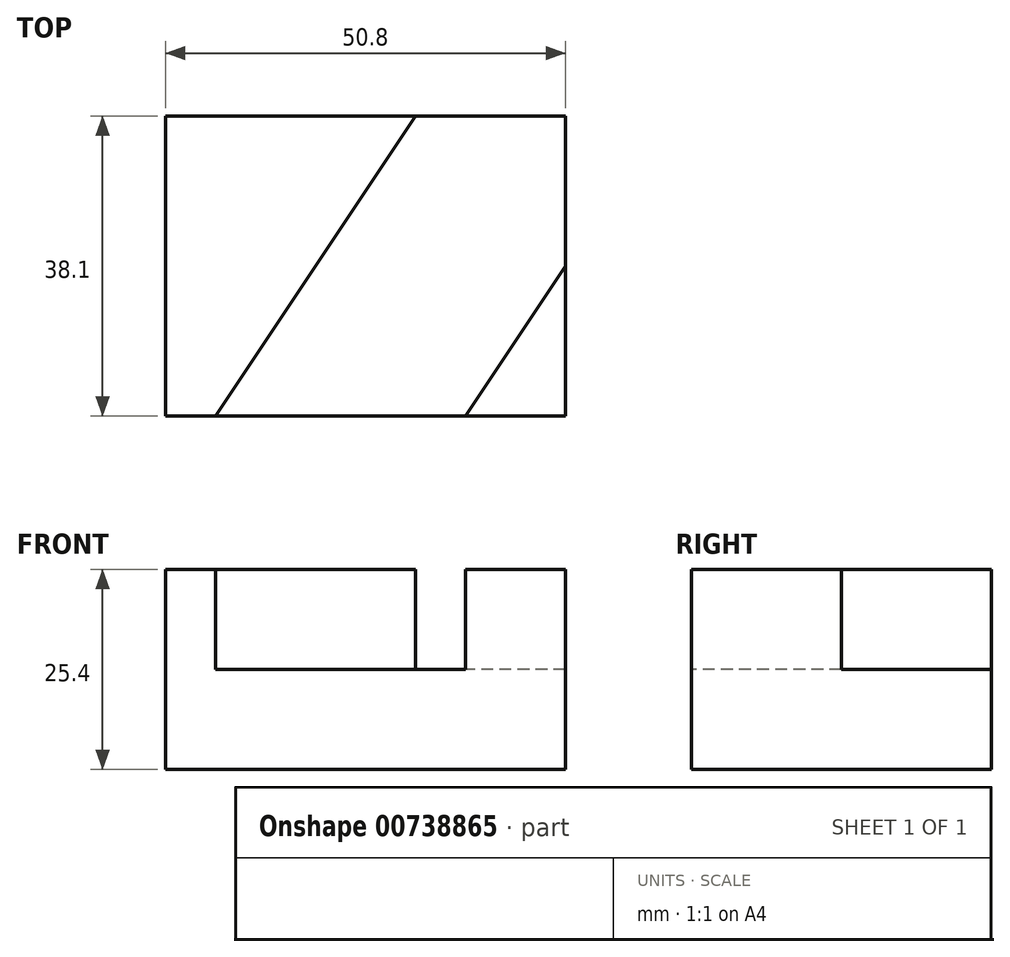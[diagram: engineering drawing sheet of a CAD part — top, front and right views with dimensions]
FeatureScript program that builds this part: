
annotation { "Feature Type Name" : "Feature", "Feature Type Description" : "" }
export const myFeature = defineFeature(function(context is Context, id is Id, definition is map)
    precondition{}
    {
        {
            var Q0;
            Q0=qCreatedBy(makeId("Front.planeOp"),FACE);
            var sketch = newSketch(context, id + "F0", { "sketchPlane" : qUnion([Q0])});
            skLineSegment(sketch, "E0", {"start": v(0, 25.4) * mm, "end": v(0, 0) * mm});
            skLineSegment(sketch, "E1", {"start": v(0, 0) * mm, "end": v(50.8, 0) * mm});
            skLineSegment(sketch, "E2", {"start": v(50.8, 0) * mm, "end": v(50.8, 25.4) * mm});
            skLineSegment(sketch, "E3", {"start": v(50.8, 25.4) * mm, "end": v(0, 25.4) * mm});
            skSolve(sketch);
        }
        {
            var Q0;
            Q0=makeQuery(id+"F0.imprint","IMPRINT",FACE,{"disambiguationData":[TD([[makeQuery(id+"F0.imprint","IMPRINT",EDGE,{"derivedFrom":sQuery(id+"F0.wireOp",EDGE,"E0")}),1.0]])]});
            extrude(context, id + "F1", {"entities" : qUnion([Q0]), "depth" : 38.1 * mm, "offsetDistance" : 25.4 * mm});
        }
        {
            var Q0;
            Q0=makeQuery(id+"F1.opExtrude","SWEPT_FACE",FACE,{"disambiguationData":[OSD([sQuery(id+"F0.wireOp",EDGE,"E3")])]});
            var sketch = newSketch(context, id + "F2", { "sketchPlane" : qUnion([Q0])});
            skLineSegment(sketch, "E4", {"start": v(31.75, 0) * mm, "end": v(6.35, -38.1) * mm});
            skLineSegment(sketch, "E5", {"start": v(50.8, -19.05) * mm, "end": v(38.1, -38.1) * mm});
            skSolve(sketch);
        }
        {
            var Q0;
            Q0 = qSketchRegion(id + "F2", true);
            var Q1;
            {var subQ5=sQuery(id+"F2.wireOp",EDGE,"E4");Q1=makeQuery(id+"F2.imprint","IMPRINT",FACE,{"disambiguationData":[TD([[makeQuery(id+"F2.imprint","IMPRINT",EDGE,{"derivedFrom":subQ5}),1.0]])]});}
            extrude(context, id + "F3", {"entities" : qUnion([Q0, Q1]), "operationType" : NewBodyOperationType.REMOVE, "oppositeDirection" : true, "depth" : 12.7 * mm, "offsetDistance" : 25.4 * mm});
        }
    });
